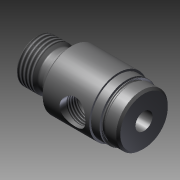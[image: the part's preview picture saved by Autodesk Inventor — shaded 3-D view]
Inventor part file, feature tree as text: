
AUTODESK INVENTOR PART (.ipt)
format: ipt  version: 2011 SP1 (Build 150282100, 282)  size: 260,096 bytes
history: native  units: in
note: dims shown in document units (in); Inventor stores cm internally (conversion verified against a paired STEP export)
features: other x119, sketch x6, revolve x5, thread x2, hole x1
ambient origin geometry x8: Origin, YZ Plane, XZ Plane, XY Plane, X Axis, Y Axis, Z Axis, Center Point
bodies: Solid1 (feature_tree)
feature tree (133):
  revolve  "Revolution1"  [1 undecoded]
  thread  "Thread1"  [1 undecoded]
  revolve  "Revolution2"  Angle=360.0deg
  hole  "Hole1"  [1 undecoded]
  revolve  "Revolution3"  [1 undecoded]
  revolve  "Revolution4"  [1 undecoded]
  thread  "Thread2"  [1 undecoded]
  revolve  "Revolution5"  [1 undecoded]
  other  "dp1_XY"
  other  "dp1_YZ"
  other  "dp1_ZX"
  other  "dp1_X"
  other  "dp1_Y"
  other  "dp1_Z"
  other  "dp1_Center"
  other  "dp2_XY"
  other  "dp2_YZ"
  other  "dp2_ZX"
  other  "dp2_X"
  other  "dp2_Y"
  other  "dp2_Z"
  other  "dp2_Center"
  other  "hh_XY"
  other  "hh_YZ"
  other  "hh_ZX"
  other  "hh_X"
  other  "hh_Y"
  other  "hh_Z"
  other  "hh_Center"
  other  "port_XY"
  other  "port_YZ"
  other  "port_ZX"
  other  "port_X"
  other  "port_Y"
  other  "port_Z"
  other  "port_Center"
  other  "rod_guide_XY"
  other  "rod_guide_YZ"
  other  "rod_guide_ZX"
  other  "rod_guide_X"
  other  "rod_guide_Y"
  other  "rod_guide_Z"
  other  "rod_guide_Center"
  other  "s1_XY"
  other  "s1_YZ"
  other  "s1_ZX"
  other  "s1_X"
  other  "s1_Y"
  other  "s1_Z"
  other  "s1_Center"
  other  "s2_XY"
  other  "s2_YZ"
  other  "s2_ZX"
  other  "s2_X"
  other  "s2_Y"
  other  "s2_Z"
  other  "s2_Center"
  other  "t1_XY"
  other  "t1_YZ"
  other  "t1_ZX"
  other  "t1_X"
  other  "t1_Y"
  other  "t1_Z"
  other  "t1_Center"
  other  "t111_XY"
  other  "t111_YZ"
  other  "t111_ZX"
  other  "t111_X"
  other  "t111_Y"
  other  "t111_Z"
  other  "t111_Center"
  other  "to_foot_bracket_XY"
  other  "to_foot_bracket_YZ"
  other  "to_foot_bracket_ZX"
  other  "to_foot_bracket_X"
  other  "to_foot_bracket_Y"
  other  "to_foot_bracket_Z"
  other  "to_foot_bracket_Center"
  other  "to_nut_XY"
  other  "to_nut_YZ"
  other  "to_nut_ZX"
  other  "to_nut_X"
  other  "to_nut_Y"
  other  "to_nut_Z"
  other  "to_nut_Center"
  other  "to_rod_XY"
  other  "to_rod_YZ"
  other  "to_rod_ZX"
  other  "to_rod_X"
  other  "to_rod_Y"
  other  "to_rod_Z"
  other  "to_rod_Center"
  other  "to_screw_XY"
  other  "to_screw_YZ"
  other  "to_screw_ZX"
  other  "to_screw_X"
  other  "to_screw_Y"
  other  "to_screw_Z"
  other  "to_screw_Center"
  other  "to_trunnion_brackets_XY"
  other  "to_trunnion_brackets_YZ"
  other  "to_trunnion_brackets_ZX"
  other  "to_trunnion_brackets_X"
  other  "to_trunnion_brackets_Y"
  other  "to_trunnion_brackets_Z"
  other  "to_trunnion_brackets_Center"
  other  "to_trunnion_brackets1_XY"
  other  "to_trunnion_brackets1_YZ"
  other  "to_trunnion_brackets1_ZX"
  other  "to_trunnion_brackets1_X"
  other  "to_trunnion_brackets1_Y"
  other  "to_trunnion_brackets1_Z"
  other  "to_trunnion_brackets1_Center"
  other  "to_trunnion_brackets2_XY"
  other  "to_trunnion_brackets2_YZ"
  other  "to_trunnion_brackets2_ZX"
  other  "to_trunnion_brackets2_X"
  other  "to_trunnion_brackets2_Y"
  other  "to_trunnion_brackets2_Z"
  other  "to_trunnion_brackets2_Center"
  other  "to_tube_XY"
  other  "to_tube_YZ"
  other  "to_tube_ZX"
  other  "to_tube_X"
  other  "to_tube_Y"
  other  "to_tube_Z"
  other  "to_tube_Center"
  sketch  "Sketch_2"  dims[d0=360.0deg d1=0.23in d2=0.0in d3=360.0deg]
  sketch  "Sketch_3"  dims[d4=0.2535in d5=0.75in d6=0.2735in d7=0.25in d8=90.0deg d9=1.594in d10=0.0in d11=360.0deg]
  sketch  "Sketch3"  dims[d12=360.0deg d13=0.1501in d14=0.0in]
  sketch  "Sketch_10"  dims[d15=360.0deg]
  sketch  "Sketch_40"  dims[d16=0.0in d17=0.0in d18=0.0in d19=0.0in d20=0.0in d21=0.0in]
  sketch  "Sketch_47"
note: 7 required parameter values undecoded (feature->parameter linkage not recoverable at this tier; creation-order binding heuristic only, values carry confidence <= 0.55)